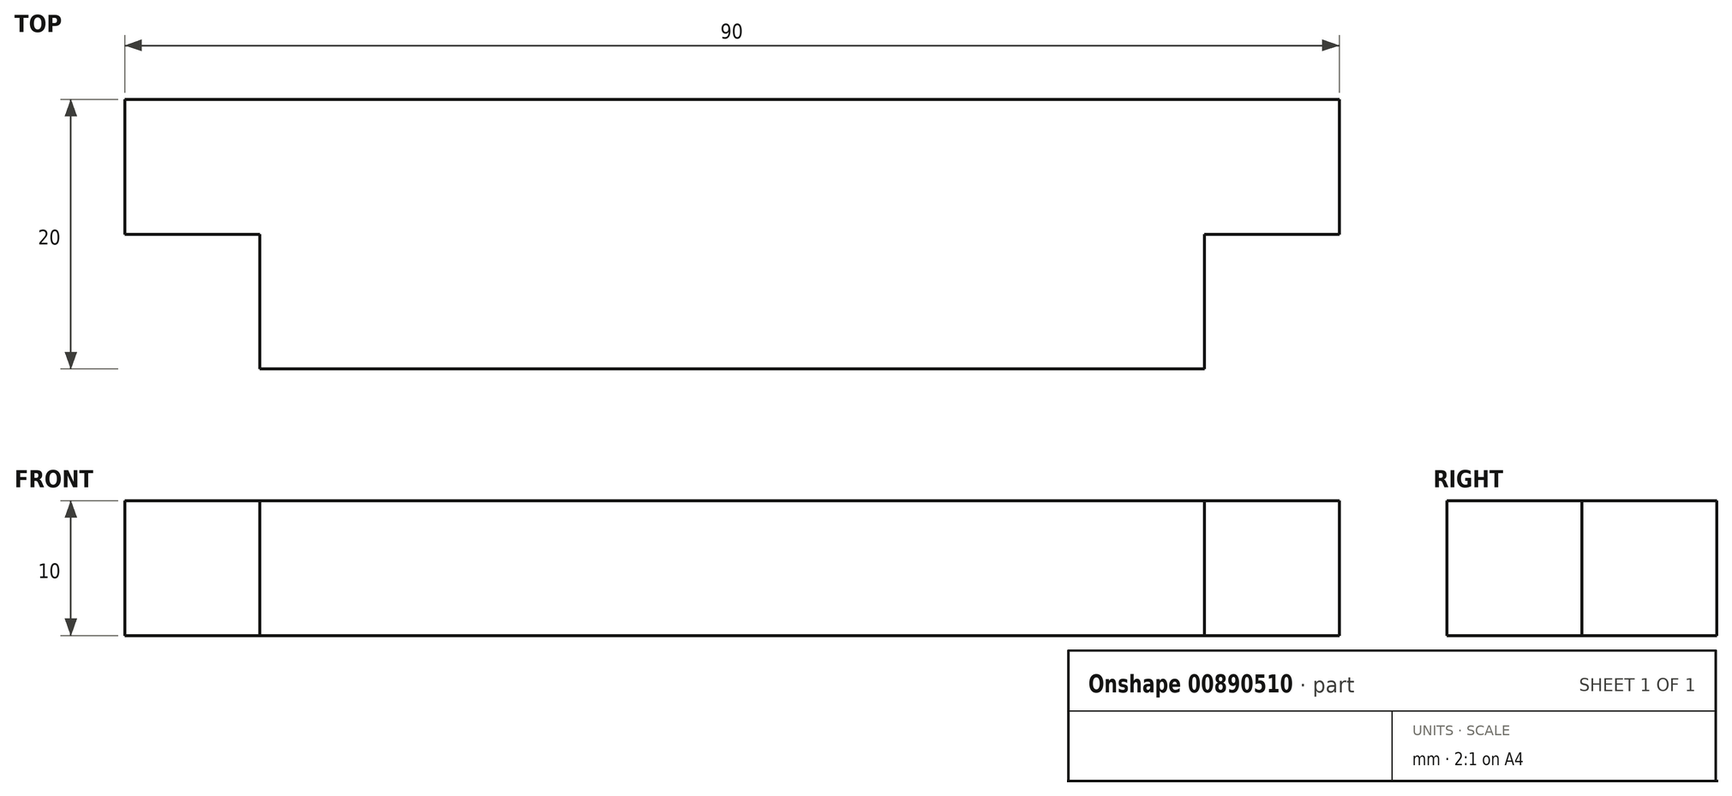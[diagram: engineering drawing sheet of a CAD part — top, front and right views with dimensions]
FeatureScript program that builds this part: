
annotation { "Feature Type Name" : "Feature", "Feature Type Description" : "" }
export const myFeature = defineFeature(function(context is Context, id is Id, definition is map)
    precondition{}
    {
        {
            var Q0;
            Q0=qCreatedBy(makeId("Top.planeOp"),FACE);
            var sketch = newSketch(context, id + "F0", { "sketchPlane" : qUnion([Q0])});
            skLineSegment(sketch, "E0.bottom", {"start": v(45, 10) * mm, "end": v(-45, 10) * mm});
            skLineSegment(sketch, "E0.top", {"start": v(35, -10) * mm, "end": v(-35, -10) * mm});
            skLineSegment(sketch, "E0.left", {"start": v(45, 10) * mm, "end": v(45, 0) * mm});
            skLineSegment(sketch, "E0.right", {"start": v(-45, 10) * mm, "end": v(-45, 0) * mm});
            skPoint(sketch, "E0.middle", {"position": v(0, 0) * mm});
            skLineSegment(sketch, "E1", {"start": v(45, 0) * mm, "end": v(35, 0) * mm});
            skLineSegment(sketch, "E2", {"start": v(35, 0) * mm, "end": v(35, -10) * mm});
            skLineSegment(sketch, "E3", {"start": v(-45, 0) * mm, "end": v(-35, 0) * mm});
            skLineSegment(sketch, "E4", {"start": v(-35, 0) * mm, "end": v(-35, -10) * mm});
            skPoint(sketch, "E5.orphan", {"position": v(-45, -10) * mm});
            skPoint(sketch, "E6.orphan", {"position": v(45, -10) * mm});
            skPoint(sketch, "E7.orphan", {"position": v(0, 10) * mm});
            skPoint(sketch, "E8.end.orphan", {"position": v(0, -10) * mm});
            skSolve(sketch);
        }
        {
            var Q0;
            Q0=makeQuery(id+"F0.imprint","IMPRINT",FACE,{"disambiguationData":[TD([[makeQuery(id+"F0.imprint","IMPRINT",EDGE,{"derivedFrom":sQuery(id+"F0.wireOp",EDGE,"E0.bottom")}),1.0]])]});
            extrude(context, id + "F1", {"entities" : qUnion([Q0]), "depth" : 10 * mm, "offsetDistance" : 25 * mm});
        }
    });
